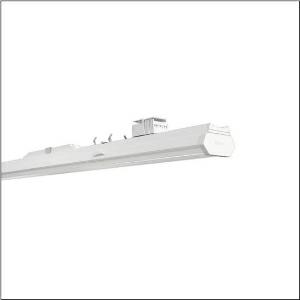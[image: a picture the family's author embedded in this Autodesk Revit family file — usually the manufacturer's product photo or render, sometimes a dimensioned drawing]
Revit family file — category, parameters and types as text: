
# Revit family: licross_r__11_protected_extreme_ho_51tp12dn4fxme_36ff
name_source: partatom
category: Lighting Fixtures
units: mm (PartAtom-declared; Revit-internal decimal feet)

## family parameters
Cut with Voids When Loaded = No
Host = Face
Light Source = No
Part Type = Normal
Room Calculation Point = No
Round Connector Dimension = Use Diameter
Shared = No

## types (1)
- --- (1 x LED, 15270 lm, 87.3 W, 4000K)
    Apparent Load = 87 VA
    CIE Flux Codes = 70 91 97 98 100
    Color Rendering = 80
    Color Temperature = 4000K
    Default Elevation = 1800 mm
    Description = Licross® 11 Protected extreme HO, luminaire insert, of sheet steel, galvanised, coil coated, white, length: 1.500mm, width: 90mm, height: 101mm, LED rated luminous flux: 15.270lm, light colour: 840, control gear: DALI 2, with plug, 5-pole, with phase selection, mains connection: 220..240V, AC, 50/60Hz, rated input power: 87W, internal wiring halogen-free, primary optical cover: cover, of PMMA, light emission: direct distribution, primary light characteristic: symmetric, protection rating (complete): IP64, insulation class (complete): insulation class I (protective earthing), certification: CE, ENEC, VDE, UKCA, protection symbol: D if used in an environment with conductive dust loads with corresponding accessories, impact resistance: IK06, permissible ambient temperature for indoor applications: -40..+40°C, corresponds to IFS (International Featured Standards) requirements for safety and quality in the food industry, reducing of maximum allowable ambient temperature of 5°C with ceiling mounting, LABS conformity tested according to VDMA 24364:2018-05, packaging unit: 1 piece
    Height = 92 mm
    Lamp = 1 x LED
    Lamp Light Flux = 15270 lm
    Lamp Power = 87.3 W
    Lamp count = 1
    Length = 1500 mm
    Luminous efficacy = 175 lm/W
    Manufacturer = Siteco
    ModVariant = No
    Model = 51TP12DN4FXME
    Mounting Place = Ceiling
    Mounting Type = Pendant
    Number of Poles = 1
    OnlyDefault = Yes
    Power Factor = 1
    Product Name = Licross® 11 Protected extreme HO
    Product group = luminaire insert | ceiling pendant
    ProductGroupID = 902
    Protection Class = Protection class I
    Protection Degree = IP 64
    RLX_Detail_Level = 1
    RLX_Emergency_Light_Flux = 0 lm
    RLX_Emergency_Type = 0
    RLX_Emergency_Type_DB = No
    RlxData = <blob elided: 24509 chars, md5=0b6f9ec0>
    Socket = socket
    Standby Power = 0 W
    System Light Flux = 15270 lm
    System Power = 87 W
    Type Comments = factory setting: luminous flux: 100 % | dim-lin: 254 | 589 mA
    Type Image = l_1256148.jpg
    URL = http://relux.com
    VarID = @adj_104217
    Voltage = 0 V
    Weight = 0.00 kg
    Width = 88 mm

## geometry (parser evidence)
native form markers: Blend x4, Sweep x9
no freeform markers — native parametric forms only
